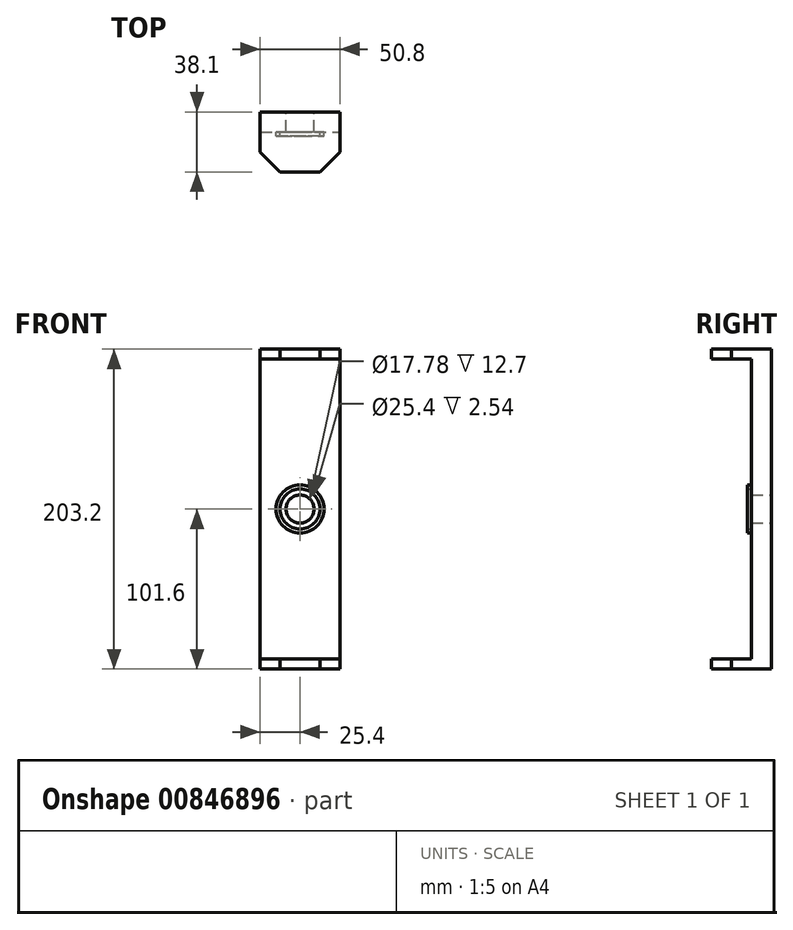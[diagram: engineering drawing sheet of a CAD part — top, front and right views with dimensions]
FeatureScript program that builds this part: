
annotation { "Feature Type Name" : "Feature", "Feature Type Description" : "" }
export const myFeature = defineFeature(function(context is Context, id is Id, definition is map)
    precondition{}
    {
        {
            var Q0;
            Q0=qCreatedBy(makeId("Front.planeOp"),FACE);
            var sketch = newSketch(context, id + "F0", { "sketchPlane" : qUnion([Q0])});
            skLineSegment(sketch, "E0.bottom", {"start": v(-25.4, 101.6) * mm, "end": v(25.4, 101.6) * mm});
            skLineSegment(sketch, "E0.top", {"start": v(-25.4, -101.6) * mm, "end": v(25.4, -101.6) * mm});
            skLineSegment(sketch, "E0.left", {"start": v(-25.4, 101.6) * mm, "end": v(-25.4, -101.6) * mm});
            skLineSegment(sketch, "E0.right", {"start": v(25.4, 101.6) * mm, "end": v(25.4, -101.6) * mm});
            skPoint(sketch, "E0.middle", {"position": v(0, 0) * mm});
            skCircle(sketch, "E1", {"center": v(0, 0) * mm, "radius": 8.9 * mm});
            skSolve(sketch);
        }
        {
            var Q0;
            Q0=makeQuery(id+"F0.imprint","IMPRINT",FACE,{"disambiguationData":[TD([[makeQuery(id+"F0.imprint","IMPRINT",EDGE,{"derivedFrom":sQuery(id+"F0.wireOp",EDGE,"E0.bottom")}),-1.0]])]});
            extrude(context, id + "F1", {"entities" : qUnion([Q0]), "depth" : 12.7 * mm, "offsetDistance" : 25.4 * mm});
        }
        {
            var Q0;
            Q0=makeQuery(id+"F1.opExtrude","CAP_FACE",FACE,{"disambiguationData":[OSD([sQuery(id+"F0.wireOp",EDGE,"E0.bottom"),sQuery(id+"F0.wireOp",EDGE,"E0.top"),sQuery(id+"F0.wireOp",EDGE,"E0.left"),sQuery(id+"F0.wireOp",EDGE,"E0.right"),sQuery(id+"F0.wireOp",EDGE,"E1")])],"isStart":false});
            var sketch = newSketch(context, id + "F2", { "sketchPlane" : qUnion([Q0])});
            skCircle(sketch, "E2", {"center": v(0, 0) * mm, "radius": 8.9 * mm});
            skCircle(sketch, "E3.0", {"center": v(0, 0) * mm, "radius": 12.7 * mm});
            skCircle(sketch, "E4.0", {"center": v(0, 0) * mm, "radius": 15.24 * mm});
            skCircle(sketch, "E5.0", {"center": v(0, 0) * mm, "radius": 19.05 * mm});
            skLineSegment(sketch, "E6", {"start": v(0, 0) * mm, "end": v(-15.24, 0) * mm});
            skLineSegment(sketch, "E7", {"start": v(-15.24, 0) * mm, "end": v(15.24, 0) * mm});
            skLineSegment(sketch, "E8", {"start": v(15.24, 0) * mm, "end": v(0, 0) * mm});
            skLineSegment(sketch, "E9", {"start": v(0, 0) * mm, "end": v(0, 15.24) * mm});
            skLineSegment(sketch, "E10", {"start": v(0, 15.24) * mm, "end": v(0, -15.24) * mm});
            skLineSegment(sketch, "E11", {"start": v(0, -15.24) * mm, "end": v(0, 0) * mm});
            skLineSegment(sketch, "E12", {"start": v(0, 0) * mm, "end": v(-13.2, -7.62) * mm});
            skLineSegment(sketch, "E13", {"start": v(0, 0) * mm, "end": v(-7.62, -13.2) * mm});
            skLineSegment(sketch, "E14.MirrorCS", {"start": v(0, 0) * mm, "end": v(7.62, -13.2) * mm});
            skLineSegment(sketch, "E15.MirrorCS", {"start": v(0, 0) * mm, "end": v(13.2, -7.62) * mm});
            skLineSegment(sketch, "E16.MirrorCS", {"start": v(0, 0) * mm, "end": v(-13.2, 7.62) * mm});
            skLineSegment(sketch, "E17.MirrorCS", {"start": v(0, 0) * mm, "end": v(-7.62, 13.2) * mm});
            skLineSegment(sketch, "E18.MirrorCS", {"start": v(0, 0) * mm, "end": v(7.62, 13.2) * mm});
            skLineSegment(sketch, "E19.MirrorCS", {"start": v(0, 0) * mm, "end": v(13.2, 7.62) * mm});
            skLineSegment(sketch, "E20", {"start": v(0, 0) * mm, "end": v(-10.78, 10.78) * mm});
            skLineSegment(sketch, "E21.MirrorCS", {"start": v(0, 0) * mm, "end": v(10.78, 10.78) * mm});
            skLineSegment(sketch, "E22", {"start": v(0, 0) * mm, "end": v(-3.94, 14.72) * mm});
            skLineSegment(sketch, "E23", {"start": v(0, 0) * mm, "end": v(-14.72, 3.94) * mm});
            skLineSegment(sketch, "E24.MirrorCS", {"start": v(0, 0) * mm, "end": v(14.72, 3.94) * mm});
            skLineSegment(sketch, "E25.MirrorCS", {"start": v(0, 0) * mm, "end": v(3.94, 14.72) * mm});
            skLineSegment(sketch, "E26.MirrorCS", {"start": v(0, 0) * mm, "end": v(-14.72, -3.94) * mm});
            skLineSegment(sketch, "E27.MirrorCS", {"start": v(0, 0) * mm, "end": v(-10.78, -10.78) * mm});
            skLineSegment(sketch, "E28.MirrorCS", {"start": v(0, 0) * mm, "end": v(-3.94, -14.72) * mm});
            skLineSegment(sketch, "E29.MirrorCS", {"start": v(0, 0) * mm, "end": v(3.94, -14.72) * mm});
            skLineSegment(sketch, "E30.MirrorCS", {"start": v(0, 0) * mm, "end": v(10.78, -10.78) * mm});
            skLineSegment(sketch, "E31.MirrorCS", {"start": v(0, 0) * mm, "end": v(14.72, -3.94) * mm});
            skSolve(sketch);
        }
        {
            var Q0;
            {var subQ0=sQuery(id+"F2.wireOp",EDGE,"E20");var subQ1=sQuery(id+"F2.wireOp",EDGE,"E3.0");var subQ2=makeQuery(id+"F2.imprint","INTERSECT",VERTEX,{"derivedFrom":[subQ1,subQ0]});Q0=makeQuery(id+"F2.imprint","IMPRINT",FACE,{"disambiguationData":[TD([[makeQuery(id+"F2.imprint","IMPRINT",EDGE,{"disambiguationData":[TD([[subQ2,-1.0]])],"derivedFrom":subQ1}),-1.0]])]});}
            var Q1;
            {var subQ0=sQuery(id+"F2.wireOp",EDGE,"E23");var subQ1=sQuery(id+"F2.wireOp",EDGE,"E3.0");var subQ2=makeQuery(id+"F2.imprint","INTERSECT",VERTEX,{"derivedFrom":[subQ1,subQ0]});Q1=makeQuery(id+"F2.imprint","IMPRINT",FACE,{"disambiguationData":[TD([[makeQuery(id+"F2.imprint","IMPRINT",EDGE,{"disambiguationData":[TD([[subQ2,-1.0]])],"derivedFrom":subQ1}),-1.0]])]});}
            var Q2;
            {var subQ0=sQuery(id+"F2.wireOp",EDGE,"E26.MirrorCS");var subQ1=sQuery(id+"F2.wireOp",EDGE,"E3.0");var subQ2=makeQuery(id+"F2.imprint","INTERSECT",VERTEX,{"derivedFrom":[subQ1,subQ0]});Q2=makeQuery(id+"F2.imprint","IMPRINT",FACE,{"disambiguationData":[TD([[makeQuery(id+"F2.imprint","IMPRINT",EDGE,{"disambiguationData":[TD([[subQ2,-1.0]])],"derivedFrom":subQ1}),-1.0]])]});}
            var Q3;
            {var subQ0=sQuery(id+"F2.wireOp",EDGE,"E27.MirrorCS");var subQ1=sQuery(id+"F2.wireOp",EDGE,"E3.0");var subQ2=makeQuery(id+"F2.imprint","INTERSECT",VERTEX,{"derivedFrom":[subQ1,subQ0]});Q3=makeQuery(id+"F2.imprint","IMPRINT",FACE,{"disambiguationData":[TD([[makeQuery(id+"F2.imprint","IMPRINT",EDGE,{"disambiguationData":[TD([[subQ2,-1.0]])],"derivedFrom":subQ1}),-1.0]])]});}
            var Q4;
            {var subQ0=sQuery(id+"F2.wireOp",EDGE,"E28.MirrorCS");var subQ1=sQuery(id+"F2.wireOp",EDGE,"E3.0");var subQ2=makeQuery(id+"F2.imprint","INTERSECT",VERTEX,{"derivedFrom":[subQ1,subQ0]});Q4=makeQuery(id+"F2.imprint","IMPRINT",FACE,{"disambiguationData":[TD([[makeQuery(id+"F2.imprint","IMPRINT",EDGE,{"disambiguationData":[TD([[subQ2,-1.0]])],"derivedFrom":subQ1}),-1.0]])]});}
            var Q5;
            {var subQ0=sQuery(id+"F2.wireOp",EDGE,"E29.MirrorCS");var subQ1=sQuery(id+"F2.wireOp",EDGE,"E3.0");var subQ2=makeQuery(id+"F2.imprint","INTERSECT",VERTEX,{"derivedFrom":[subQ1,subQ0]});Q5=makeQuery(id+"F2.imprint","IMPRINT",FACE,{"disambiguationData":[TD([[makeQuery(id+"F2.imprint","IMPRINT",EDGE,{"disambiguationData":[TD([[subQ2,-1.0]])],"derivedFrom":subQ1}),-1.0]])]});}
            var Q6;
            {var subQ0=sQuery(id+"F2.wireOp",EDGE,"E30.MirrorCS");var subQ1=sQuery(id+"F2.wireOp",EDGE,"E3.0");var subQ2=makeQuery(id+"F2.imprint","INTERSECT",VERTEX,{"derivedFrom":[subQ1,subQ0]});Q6=makeQuery(id+"F2.imprint","IMPRINT",FACE,{"disambiguationData":[TD([[makeQuery(id+"F2.imprint","IMPRINT",EDGE,{"disambiguationData":[TD([[subQ2,-1.0]])],"derivedFrom":subQ1}),-1.0]])]});}
            var Q7;
            {var subQ0=sQuery(id+"F2.wireOp",EDGE,"E8");var subQ1=sQuery(id+"F2.wireOp",EDGE,"E3.0");var subQ2=makeQuery(id+"F2.imprint","INTERSECT",VERTEX,{"derivedFrom":[subQ1,subQ0]});Q7=makeQuery(id+"F2.imprint","IMPRINT",FACE,{"disambiguationData":[TD([[makeQuery(id+"F2.imprint","IMPRINT",EDGE,{"disambiguationData":[TD([[subQ2,1.0]])],"derivedFrom":subQ1}),-1.0]])]});}
            var Q8;
            {var subQ0=sQuery(id+"F2.wireOp",EDGE,"E24.MirrorCS");var subQ1=sQuery(id+"F2.wireOp",EDGE,"E3.0");var subQ2=makeQuery(id+"F2.imprint","INTERSECT",VERTEX,{"derivedFrom":[subQ1,subQ0]});Q8=makeQuery(id+"F2.imprint","IMPRINT",FACE,{"disambiguationData":[TD([[makeQuery(id+"F2.imprint","IMPRINT",EDGE,{"disambiguationData":[TD([[subQ2,-1.0]])],"derivedFrom":subQ1}),-1.0]])]});}
            var Q9;
            {var subQ0=sQuery(id+"F2.wireOp",EDGE,"E21.MirrorCS");var subQ1=sQuery(id+"F2.wireOp",EDGE,"E3.0");var subQ2=makeQuery(id+"F2.imprint","INTERSECT",VERTEX,{"derivedFrom":[subQ1,subQ0]});Q9=makeQuery(id+"F2.imprint","IMPRINT",FACE,{"disambiguationData":[TD([[makeQuery(id+"F2.imprint","IMPRINT",EDGE,{"disambiguationData":[TD([[subQ2,-1.0]])],"derivedFrom":subQ1}),-1.0]])]});}
            var Q10;
            {var subQ0=sQuery(id+"F2.wireOp",EDGE,"E25.MirrorCS");var subQ1=sQuery(id+"F2.wireOp",EDGE,"E3.0");var subQ2=makeQuery(id+"F2.imprint","INTERSECT",VERTEX,{"derivedFrom":[subQ1,subQ0]});Q10=makeQuery(id+"F2.imprint","IMPRINT",FACE,{"disambiguationData":[TD([[makeQuery(id+"F2.imprint","IMPRINT",EDGE,{"disambiguationData":[TD([[subQ2,-1.0]])],"derivedFrom":subQ1}),-1.0]])]});}
            var Q11;
            {var subQ0=sQuery(id+"F2.wireOp",EDGE,"E22");var subQ1=sQuery(id+"F2.wireOp",EDGE,"E3.0");var subQ2=makeQuery(id+"F2.imprint","INTERSECT",VERTEX,{"derivedFrom":[subQ1,subQ0]});Q11=makeQuery(id+"F2.imprint","IMPRINT",FACE,{"disambiguationData":[TD([[makeQuery(id+"F2.imprint","IMPRINT",EDGE,{"disambiguationData":[TD([[subQ2,-1.0]])],"derivedFrom":subQ1}),-1.0]])]});}
            extrude(context, id + "F3", {"entities" : qUnion([Q0, Q1, Q2, Q3, Q4, Q5, Q6, Q7, Q8, Q9, Q10, Q11]), "operationType" : NewBodyOperationType.ADD, "depth" : 2.54 * mm, "offsetDistance" : 25.4 * mm});
        }
        {
            var Q0;
            Q0=makeQuery(id+"F1.opExtrude","CAP_FACE",FACE,{"disambiguationData":[OSD([sQuery(id+"F0.wireOp",EDGE,"E0.bottom"),sQuery(id+"F0.wireOp",EDGE,"E0.top"),sQuery(id+"F0.wireOp",EDGE,"E0.left"),sQuery(id+"F0.wireOp",EDGE,"E0.right"),sQuery(id+"F0.wireOp",EDGE,"E1")])],"isStart":false});
            var sketch = newSketch(context, id + "F4", { "sketchPlane" : qUnion([Q0])});
            skLineSegment(sketch, "E32.bottom", {"start": v(-25.4, 101.6) * mm, "end": v(25.4, 101.6) * mm});
            skLineSegment(sketch, "E32.top", {"start": v(-25.4, 95.25) * mm, "end": v(25.4, 95.25) * mm});
            skLineSegment(sketch, "E32.left", {"start": v(-25.4, 101.6) * mm, "end": v(-25.4, 95.25) * mm});
            skLineSegment(sketch, "E32.right", {"start": v(25.4, 101.6) * mm, "end": v(25.4, 95.25) * mm});
            skLineSegment(sketch, "E33.MirrorCS", {"start": v(-25.4, -95.25) * mm, "end": v(25.4, -95.25) * mm});
            skLineSegment(sketch, "E34.MirrorCS", {"start": v(-25.4, -101.6) * mm, "end": v(-25.4, -95.25) * mm});
            skLineSegment(sketch, "E35.MirrorCS", {"start": v(25.4, -101.6) * mm, "end": v(25.4, -95.25) * mm});
            skLineSegment(sketch, "E36.MirrorCS", {"start": v(-25.4, -101.6) * mm, "end": v(25.4, -101.6) * mm});
            skSolve(sketch);
        }
        {
            var Q0;
            Q0 = qSketchRegion(id + "F4", true);
            extrude(context, id + "F5", {"entities" : qUnion([Q0]), "operationType" : NewBodyOperationType.ADD, "depth" : 25.4 * mm, "offsetDistance" : 25.4 * mm});
        }
        {
            var Q0;
            Q0=makeQuery(id+"F5.opExtrude","CAP_EDGE",EDGE,{"disambiguationData":[OSD([sQuery(id+"F4.wireOp",EDGE,"E34.MirrorCS")])],"isStart":false});
            var Q1;
            Q1=makeQuery(id+"F5.opExtrude","CAP_EDGE",EDGE,{"disambiguationData":[OSD([sQuery(id+"F4.wireOp",EDGE,"E35.MirrorCS")])],"isStart":false});
            var Q2;
            Q2=makeQuery(id+"F5.opExtrude","CAP_EDGE",EDGE,{"disambiguationData":[OSD([sQuery(id+"F4.wireOp",EDGE,"E32.right")])],"isStart":false});
            var Q3;
            Q3=makeQuery(id+"F5.opExtrude","CAP_EDGE",EDGE,{"disambiguationData":[OSD([sQuery(id+"F4.wireOp",EDGE,"E32.left")])],"isStart":false});
            chamfer(context, id + "F6", {"entities" : qUnion([Q0, Q1, Q2, Q3]), "width" : 12.7 * mm, "tangentPropagation" : true});
        }
    });
